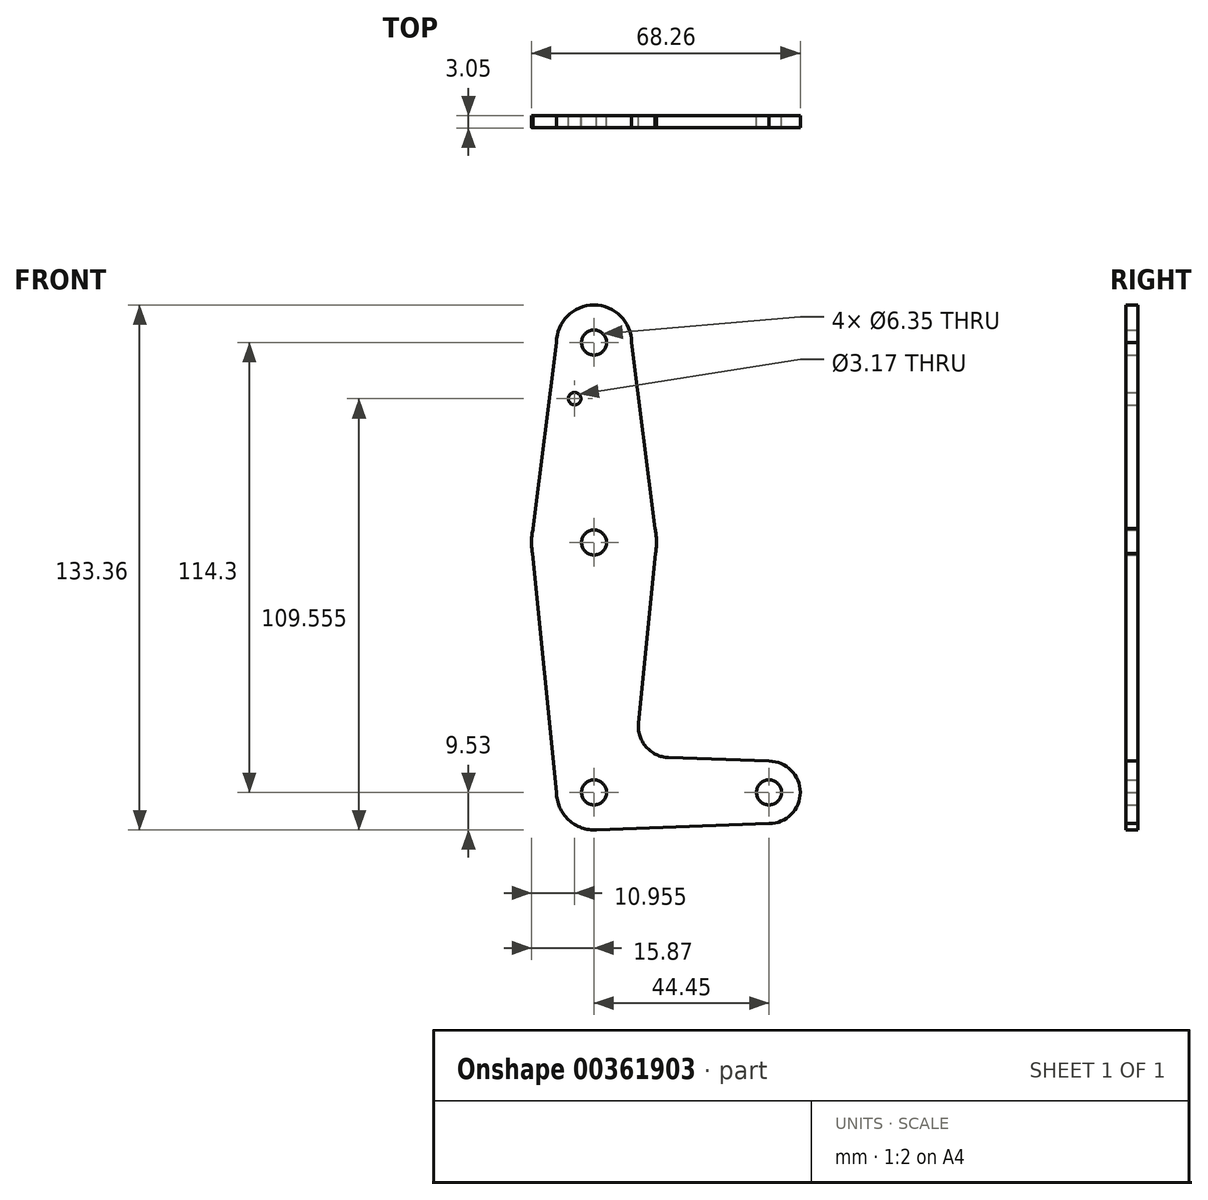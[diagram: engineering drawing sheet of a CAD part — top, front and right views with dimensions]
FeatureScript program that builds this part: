
annotation { "Feature Type Name" : "Feature", "Feature Type Description" : "" }
export const myFeature = defineFeature(function(context is Context, id is Id, definition is map)
    precondition{}
    {
        {
            var Q0;
            Q0=qCreatedBy(makeId("Front.planeOp"),FACE);
            var sketch = newSketch(context, id + "F0", { "sketchPlane" : qUnion([Q0])});
            skLineSegment(sketch, "E0", {"start": v(0, 0) * mm, "end": v(0, 114.3) * mm, "construction": true});
            skLineSegment(sketch, "E1", {"start": v(0, 0) * mm, "end": v(44.45, 0) * mm, "construction": true});
            skCircle(sketch, "E2", {"center": v(0, 114.3) * mm, "radius": 9.53 * mm});
            skCircle(sketch, "E3", {"center": v(44.45, 0) * mm, "radius": 7.94 * mm});
            skCircle(sketch, "E4", {"center": v(0, 0) * mm, "radius": 9.53 * mm});
            skCircle(sketch, "E5", {"center": v(0, 63.5) * mm, "radius": 15.88 * mm});
            skLineSegment(sketch, "E6", {"start": v(44.45, 7.94) * mm, "end": v(18.92, 8.85) * mm});
            skLineSegment(sketch, "E7", {"start": v(0, -9.52) * mm, "end": v(44.45, -7.94) * mm});
            skCircle(sketch, "E8", {"center": v(0, 114.3) * mm, "radius": 3.18 * mm});
            skCircle(sketch, "E9", {"center": v(0, 0) * mm, "radius": 3.18 * mm});
            skCircle(sketch, "E10", {"center": v(44.45, 0) * mm, "radius": 3.18 * mm});
            skCircle(sketch, "E11", {"center": v(0, 63.5) * mm, "radius": 3.18 * mm});
            skLineSegment(sketch, "E12", {"start": v(-9.53, 114.3) * mm, "end": v(-15.87, 63.9) * mm});
            skLineSegment(sketch, "E13.MirrorCS", {"start": v(9.53, 114.3) * mm, "end": v(15.87, 63.9) * mm});
            skLineSegment(sketch, "E14", {"start": v(-9.52, 0) * mm, "end": v(-15.87, 63.1) * mm});
            skLineSegment(sketch, "E15.MirrorCS", {"start": v(11.3, 17.6) * mm, "end": v(15.87, 63.1) * mm});
            skPoint(sketch, "E16.newPointB", {"position": v(9.52, 0) * mm});
            skArc(sketch, "E16.filletArc", {"start": v(11.3, 17.6) * mm, "mid": v(13.21, 11.57) * mm, "end": v(18.92, 8.85) * mm});
            skCircle(sketch, "E17", {"center": v(-4.91, 100.03) * mm, "radius": 1.59 * mm});
            skSolve(sketch);
        }
        {
            var Q0;
            Q0 = qSketchRegion(id + "F0", true);
            extrude(context, id + "F1", {"entities" : qUnion([Q0]), "depth" : 3.05 * mm});
        }
    });
